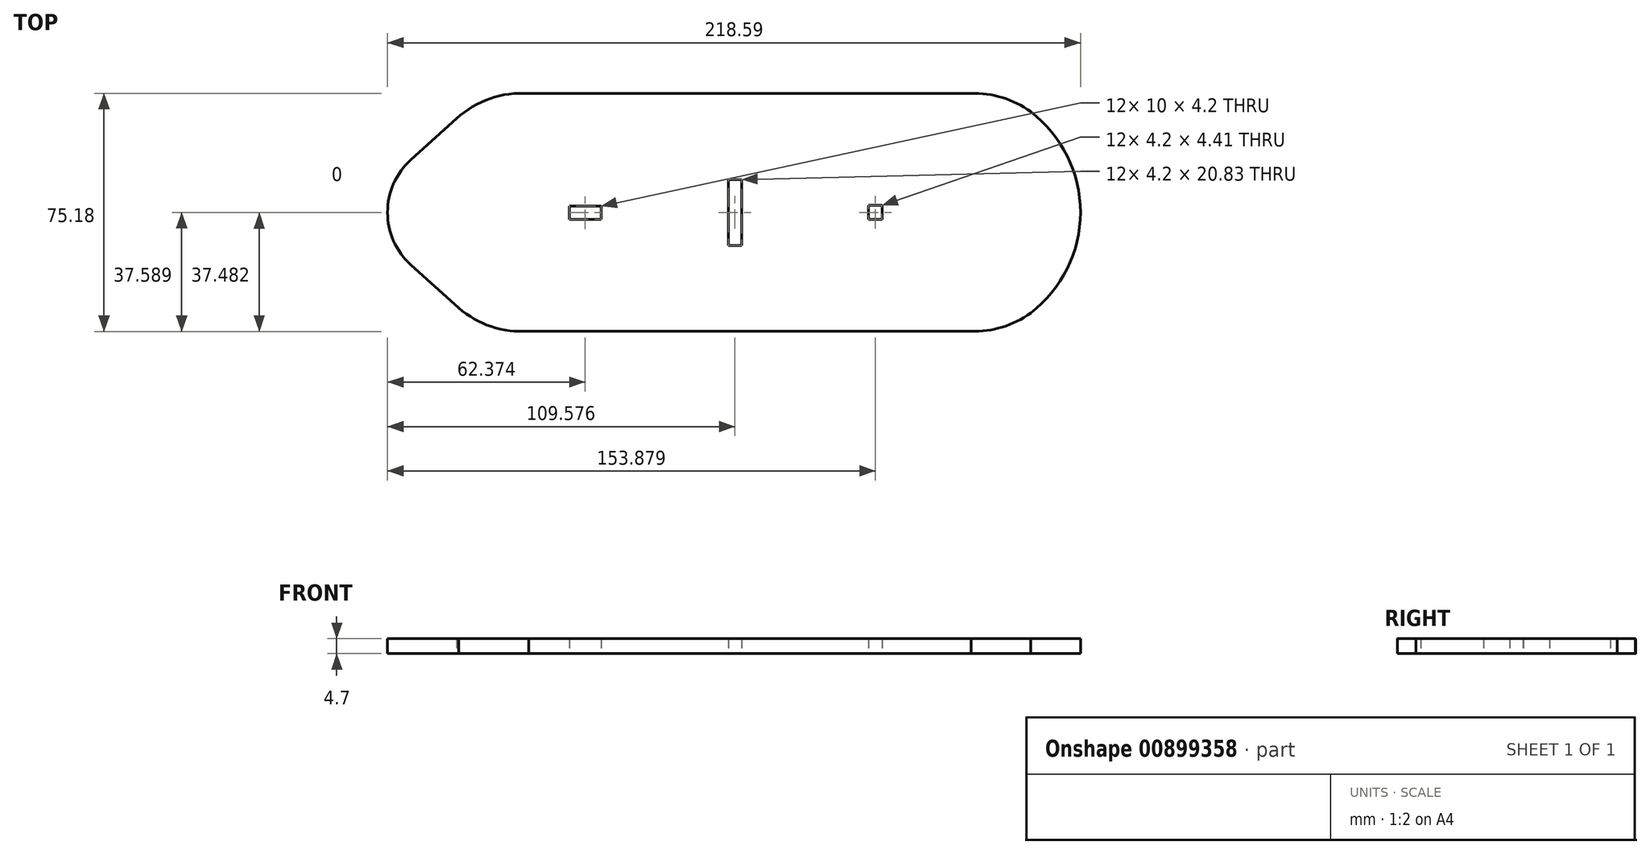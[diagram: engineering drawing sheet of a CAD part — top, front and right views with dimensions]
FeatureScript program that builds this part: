
annotation { "Feature Type Name" : "Feature", "Feature Type Description" : "" }
export const myFeature = defineFeature(function(context is Context, id is Id, definition is map)
    precondition{}
    {
        {
            var Q0;
            Q0=qCreatedBy(makeId("Top.planeOp"),FACE);
            var sketch = newSketch(context, id + "F0", { "sketchPlane" : qUnion([Q0])});
            skPoint(sketch, "E0.middle", {"position": v(7.2, 0.19) * mm});
            skPoint(sketch, "E1.endSnap0", {"position": v(-67.8, 0.19) * mm});
            skPoint(sketch, "E2", {"position": v(3.5, 0.19) * mm});
            skPoint(sketch, "E3.orphan", {"position": v(-87.23, 0.19) * mm});
            skPoint(sketch, "E4", {"position": v(-43.7, 0.08) * mm});
            skPoint(sketch, "E5", {"position": v(48, 0.19) * mm});
            skLineSegment(sketch, "E6.bottom", {"start": v(-48.7, 2.18) * mm, "end": v(-38.7, 2.18) * mm});
            skLineSegment(sketch, "E6.top", {"start": v(-48.7, -2.02) * mm, "end": v(-38.7, -2.02) * mm});
            skLineSegment(sketch, "E6.left", {"start": v(-48.7, 2.18) * mm, "end": v(-48.7, -2.02) * mm});
            skLineSegment(sketch, "E6.right", {"start": v(-38.7, 2.18) * mm, "end": v(-38.7, -2.02) * mm});
            skLineSegment(sketch, "E7.MirrorCS", {"start": v(45.7, 2.4) * mm, "end": v(45.7, -2.02) * mm});
            skLineSegment(sketch, "E8.MirrorCS", {"start": v(49.9, 2.4) * mm, "end": v(45.7, 2.4) * mm});
            skLineSegment(sketch, "E9.MirrorCS", {"start": v(49.9, 2.4) * mm, "end": v(49.9, -2.02) * mm});
            skLineSegment(sketch, "E10.MirrorCS", {"start": v(49.9, -2.02) * mm, "end": v(45.7, -2.02) * mm});
            skLineSegment(sketch, "E11.bottom", {"start": v(1.4, 10.6) * mm, "end": v(5.6, 10.6) * mm});
            skLineSegment(sketch, "E11.top", {"start": v(1.4, -10.23) * mm, "end": v(5.6, -10.23) * mm});
            skLineSegment(sketch, "E11.left", {"start": v(1.4, 10.6) * mm, "end": v(1.4, -10.23) * mm});
            skLineSegment(sketch, "E11.right", {"start": v(5.6, 10.6) * mm, "end": v(5.6, -10.23) * mm});
            skPoint(sketch, "E12.orphan", {"position": v(-67.8, 17.69) * mm});
            skPoint(sketch, "E13.orphan", {"position": v(-67.8, -17.31) * mm});
            skArc(sketch, "E14.4", {"start": v(87.9, 19.89) * mm, "mid": v(87.87, 19.91) * mm, "end": v(87.84, 19.94) * mm});
            skArc(sketch, "E15.0", {"start": v(-61.6, 37.69) * mm, "mid": v(-73.33, 36.26) * mm, "end": v(-83.59, 30.39) * mm});
            skLineSegment(sketch, "E15.1", {"start": v(-83.59, 30.39) * mm, "end": v(-98.7, 16.77) * mm});
            skLineSegment(sketch, "E15.2", {"start": v(-61.6, 37.69) * mm, "end": v(78, 37.69) * mm});
            skArc(sketch, "E15.3", {"start": v(-98.7, 16.77) * mm, "mid": v(-106.08, 0.19) * mm, "end": v(-98.7, -16.4) * mm});
            skLineSegment(sketch, "E15.4", {"start": v(-98.7, -16.4) * mm, "end": v(-83.59, -30) * mm});
            skArc(sketch, "E15.5", {"start": v(-61.6, -37.31) * mm, "mid": v(-73.33, -35.88) * mm, "end": v(-83.59, -30) * mm});
            skArc(sketch, "E15.6", {"start": v(96.8, 31.98) * mm, "mid": v(87.87, 36.41) * mm, "end": v(78, 37.69) * mm});
            skArc(sketch, "E15.7", {"start": v(96.8, -31.6) * mm, "mid": v(112.51, 0.19) * mm, "end": v(96.8, 31.98) * mm});
            skArc(sketch, "E15.8", {"start": v(96.8, -31.6) * mm, "mid": v(87.87, -36.04) * mm, "end": v(78, -37.31) * mm});
            skLineSegment(sketch, "E15.9", {"start": v(-61.6, -37.31) * mm, "end": v(78, -37.31) * mm});
            skLineSegment(sketch, "E16.0", {"start": v(-61.6, 37.69) * mm, "end": v(77.9, 37.69) * mm});
            skArc(sketch, "E16.1", {"start": v(-61.6, 37.69) * mm, "mid": v(-73.75, 36.11) * mm, "end": v(-84.26, 29.79) * mm});
            skLineSegment(sketch, "E16.2", {"start": v(-84.26, 29.79) * mm, "end": v(-98.7, 16.77) * mm});
            skLineSegment(sketch, "E17.trimOffspring", {"start": v(82.2, -16.86) * mm, "end": v(82.2, -17.31) * mm});
            skPoint(sketch, "E18.MirrorCS.end.orphan", {"position": v(78.47, -17.31) * mm});
            skPoint(sketch, "E19.orphan", {"position": v(84.87, -15.54) * mm});
            skPoint(sketch, "E20.orphan", {"position": v(84.87, 15.92) * mm});
            skPoint(sketch, "E21.end.orphan", {"position": v(78.47, 17.69) * mm});
            skSolve(sketch);
        }
        {
            var Q0;
            Q0 = qSketchRegion(id + "F0", true);
            var Q1;
            Q1=makeQuery(id+"F0.imprint","IMPRINT",FACE,{"disambiguationData":[TD([[makeQuery(id+"F0.imprint","IMPRINT",EDGE,{"derivedFrom":sQuery(id+"F0.wireOp",EDGE,"E6.bottom")}),1.0]])]});
            extrude(context, id + "F1", {"entities" : qUnion([Q0, Q1]), "depth" : 4.7 * mm, "offsetDistance" : 25 * mm});
        }
    });
